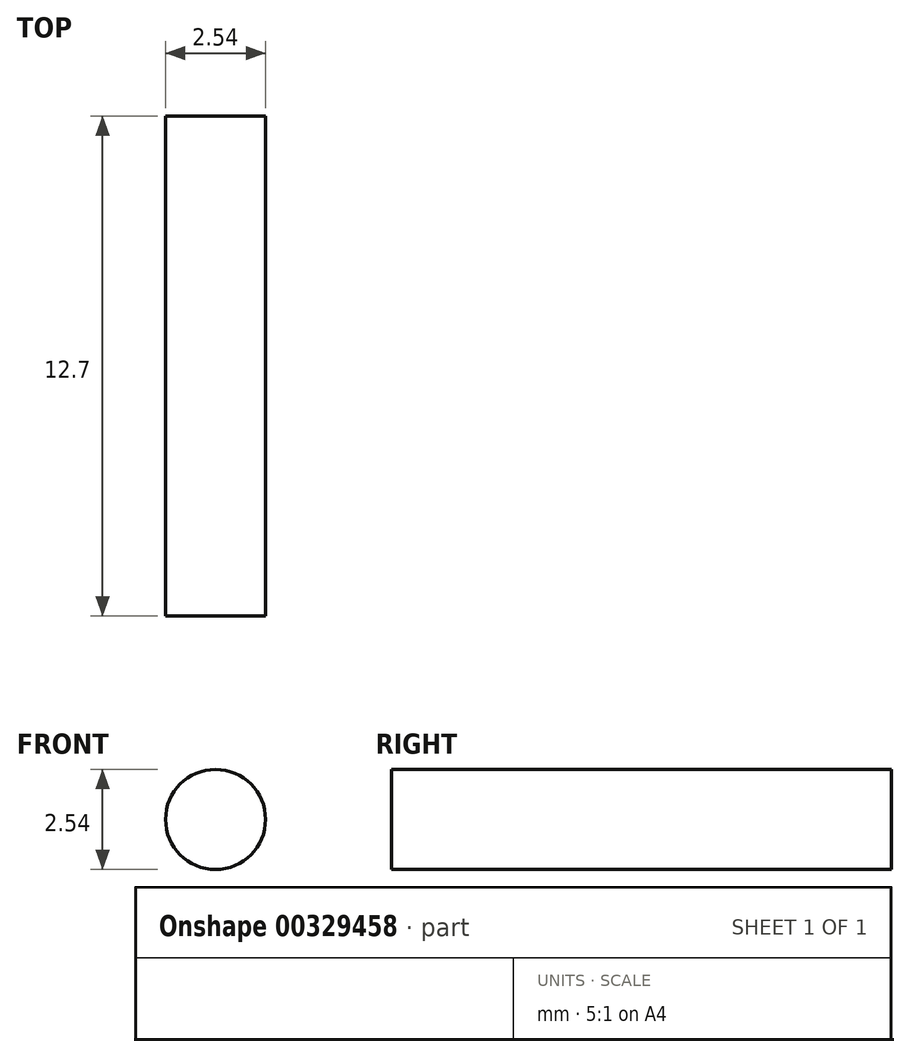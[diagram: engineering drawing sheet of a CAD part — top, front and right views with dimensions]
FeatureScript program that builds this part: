
annotation { "Feature Type Name" : "Feature", "Feature Type Description" : "" }
export const myFeature = defineFeature(function(context is Context, id is Id, definition is map)
    precondition{}
    {
        {
            var Q0;
            Q0=qCreatedBy(makeId("Front.planeOp"),FACE);
            var sketch = newSketch(context, id + "F0", { "sketchPlane" : qUnion([Q0])});
            skCircle(sketch, "E0", {"center": v(0, 0) * mm, "radius": 1.27 * mm});
            skSolve(sketch);
        }
        {
            var Q0;
            Q0 = qSketchRegion(id + "F0", true);
            extrude(context, id + "F1", {"entities" : qUnion([Q0]), "depth" : 12.7 * mm});
        }
    });
